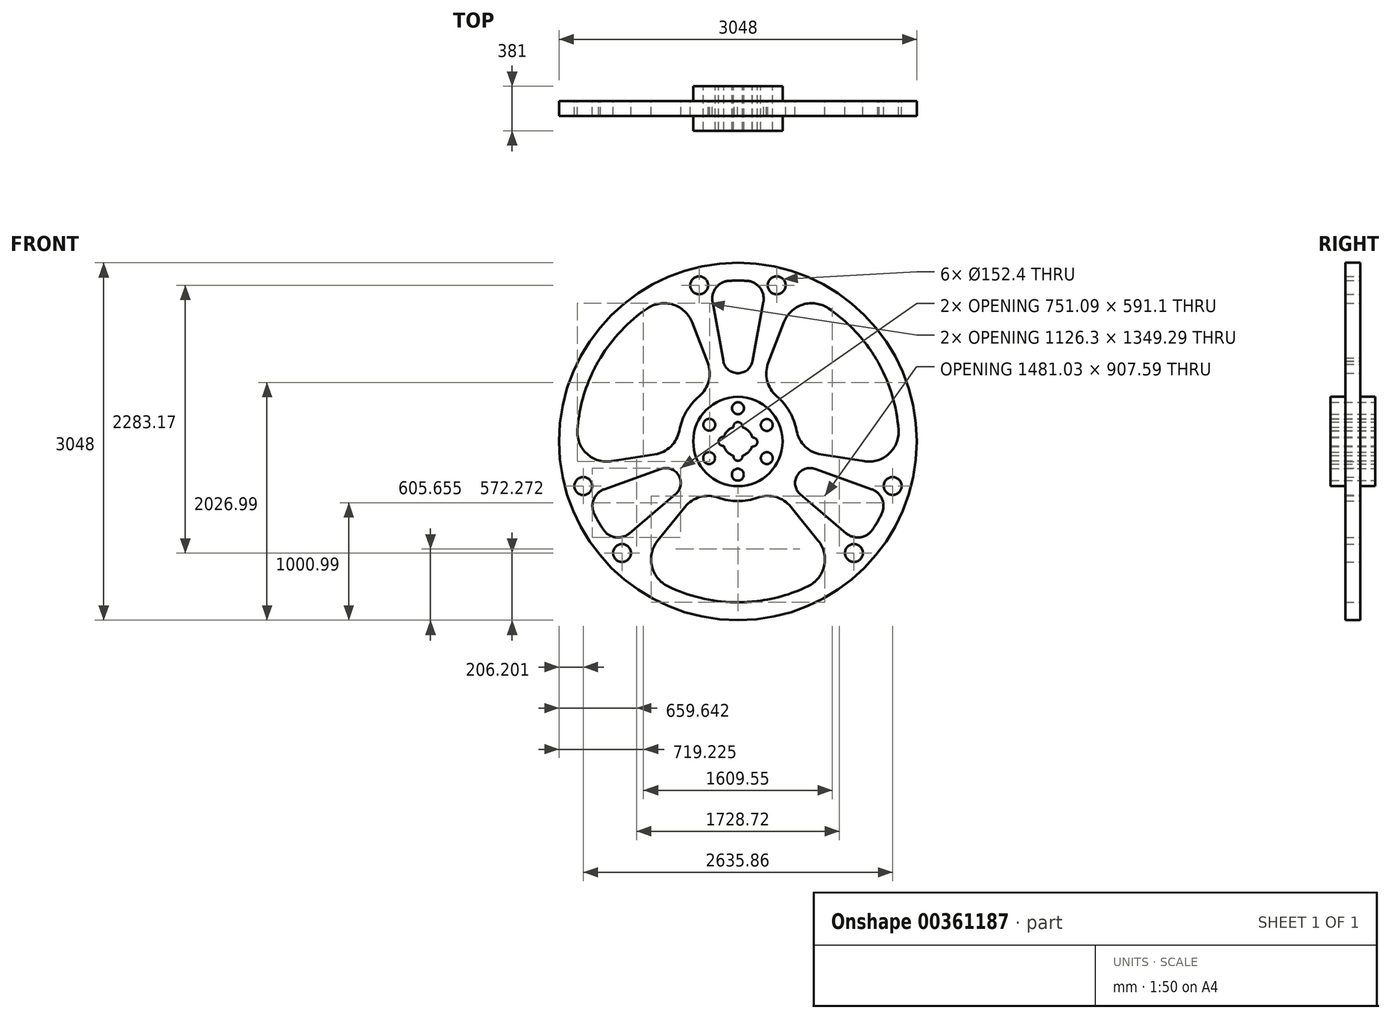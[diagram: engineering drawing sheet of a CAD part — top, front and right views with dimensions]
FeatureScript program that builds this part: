
annotation { "Feature Type Name" : "Feature", "Feature Type Description" : "" }
export const myFeature = defineFeature(function(context is Context, id is Id, definition is map)
    precondition{}
    {
        {
            var Q0;
            Q0=qCreatedBy(makeId("Front.planeOp"),FACE);
            var sketch = newSketch(context, id + "F0", { "sketchPlane" : qUnion([Q0])});
            skArc(sketch, "E0", {"start": v(75.11, 1369.54) * mm, "mid": v(0, 1371.6) * mm, "end": v(-75.11, 1369.54) * mm});
            skCircle(sketch, "E1", {"center": v(0, 0) * mm, "radius": 1524 * mm});
            skLineSegment(sketch, "E2", {"start": v(124.95, 686.17) * mm, "end": v(216.7, 1190.07) * mm});
            skLineSegment(sketch, "E3", {"start": v(-124.95, 686.17) * mm, "end": v(-216.7, 1190.07) * mm});
            skArc(sketch, "E4", {"start": v(216.7, 1190.07) * mm, "mid": v(186.42, 1311.76) * mm, "end": v(75.11, 1369.54) * mm});
            skArc(sketch, "E5", {"start": v(-75.11, 1369.54) * mm, "mid": v(-186.42, 1311.76) * mm, "end": v(-216.7, 1190.07) * mm});
            skArc(sketch, "E6", {"start": v(-124.95, 686.17) * mm, "mid": v(0, 581.92) * mm, "end": v(124.95, 686.17) * mm});
            skLineSegment(sketch, "E7", {"start": v(-0.65, -508) * mm, "end": v(-2.09, -1524) * mm});
            skPoint(sketch, "E7.endSnap0", {"position": v(-2.18, -1372.14) * mm});
            skLineSegment(sketch, "E8", {"start": v(0, 0) * mm, "end": v(-239.47, -296.33) * mm});
            skLineSegment(sketch, "E9", {"start": v(0, 0) * mm, "end": v(239.47, -296.33) * mm});
            skArc(sketch, "E10", {"start": v(-169.33, -478.95) * mm, "mid": v(0, -508) * mm, "end": v(169.33, -478.95) * mm});
            skArc(sketch, "E11", {"start": v(597.09, -1234.82) * mm, "mid": v(734.38, -1061.67) * mm, "end": v(684.07, -846.5) * mm});
            skArc(sketch, "E12", {"start": v(451.56, -558.77) * mm, "mid": v(323.13, -474) * mm, "end": v(169.33, -478.95) * mm});
            skArc(sketch, "E13", {"start": v(-169.33, -478.95) * mm, "mid": v(-323.13, -474) * mm, "end": v(-451.56, -558.77) * mm});
            skArc(sketch, "E14", {"start": v(-684.07, -846.5) * mm, "mid": v(-734.38, -1061.67) * mm, "end": v(-597.09, -1234.82) * mm});
            skLineSegment(sketch, "E15", {"start": v(-94.07, 1367.3) * mm, "end": v(-75.11, 1369.54) * mm});
            skLineSegment(sketch, "E16", {"start": v(75.11, 1369.54) * mm, "end": v(94.07, 1367.3) * mm});
            skPoint(sketch, "E17.orphan", {"position": v(-698.5, 2222.44) * mm});
            skPoint(sketch, "E18.trimOffspring.end.orphan", {"position": v(-292.1, 1604.1) * mm});
            skPoint(sketch, "E19.orphan", {"position": v(0, 1690.94) * mm});
            skPoint(sketch, "E20.trimOffspring.end.orphan", {"position": v(292.1, 1604.17) * mm});
            skPoint(sketch, "E21.orphan", {"position": v(698.5, 2211.47) * mm});
            skCircle(sketch, "E22", {"center": v(-330.38, 1331.22) * mm, "radius": 76.2 * mm});
            skCircle(sketch, "E23", {"center": v(329.48, 1331.44) * mm, "radius": 76.2 * mm});
            skArc(sketch, "E24.trimOffspring", {"start": v(-770.84, 1134.5) * mm, "mid": v(-1187.84, 685.8) * mm, "end": v(-1367.93, 100.31) * mm});
            skLineSegment(sketch, "E25.trimOffspring", {"start": v(451.56, -558.77) * mm, "end": v(684.07, -846.5) * mm});
            skLineSegment(sketch, "E26.trimOffspring", {"start": v(-451.56, -558.77) * mm, "end": v(-684.07, -846.5) * mm});
            skPoint(sketch, "E27.trimOffspring.end.orphan", {"position": v(-1005.48, -1241.52) * mm});
            skPoint(sketch, "E28.trimOffspring.end.orphan", {"position": v(1001.12, -1241.52) * mm});
            skPoint(sketch, "E29.orphan", {"position": v(-2.18, -1585.86) * mm});
            skPoint(sketch, "E30.orphan", {"position": v(0, -47.86) * mm});
            skLineSegment(sketch, "E31", {"start": v(-0.65, -508) * mm, "end": v(-0.43, -333.85) * mm});
            skArc(sketch, "E32.1.0", {"start": v(-1138.98, -407.37) * mm, "mid": v(-1229.23, -494.44) * mm, "end": v(-1223.61, -619.72) * mm});
            skLineSegment(sketch, "E32.1.1", {"start": v(-656.71, -234.88) * mm, "end": v(-1138.98, -407.37) * mm});
            skArc(sketch, "E32.1.2", {"start": v(-531.77, -451.3) * mm, "mid": v(-503.96, -290.96) * mm, "end": v(-656.71, -234.88) * mm});
            skLineSegment(sketch, "E32.1.3", {"start": v(-531.77, -451.3) * mm, "end": v(-922.28, -782.7) * mm});
            skArc(sketch, "E32.1.4", {"start": v(-1148.5, -749.82) * mm, "mid": v(-1042.81, -817.32) * mm, "end": v(-922.28, -782.7) * mm});
            skArc(sketch, "E32.1.5", {"start": v(-1223.61, -619.72) * mm, "mid": v(-1187.84, -685.8) * mm, "end": v(-1148.5, -749.82) * mm});
            skCircle(sketch, "E32.1.6", {"center": v(-987.67, -951.73) * mm, "radius": 76.2 * mm});
            skCircle(sketch, "E32.1.7", {"center": v(-1317.8, -380.39) * mm, "radius": 76.2 * mm});
            skArc(sketch, "E32.2.0", {"start": v(922.28, -782.7) * mm, "mid": v(1042.81, -817.32) * mm, "end": v(1148.5, -749.82) * mm});
            skLineSegment(sketch, "E32.2.1", {"start": v(531.77, -451.3) * mm, "end": v(922.28, -782.7) * mm});
            skArc(sketch, "E32.2.2", {"start": v(656.71, -234.88) * mm, "mid": v(503.96, -290.96) * mm, "end": v(531.77, -451.3) * mm});
            skLineSegment(sketch, "E32.2.3", {"start": v(656.71, -234.88) * mm, "end": v(1138.98, -407.37) * mm});
            skArc(sketch, "E32.2.4", {"start": v(1223.61, -619.72) * mm, "mid": v(1229.23, -494.44) * mm, "end": v(1138.98, -407.37) * mm});
            skArc(sketch, "E32.2.5", {"start": v(1148.5, -749.82) * mm, "mid": v(1187.84, -685.8) * mm, "end": v(1223.61, -619.72) * mm});
            skCircle(sketch, "E32.2.6", {"center": v(1318.06, -379.49) * mm, "radius": 76.2 * mm});
            skCircle(sketch, "E32.2.7", {"center": v(988.32, -951.05) * mm, "radius": 76.2 * mm});
            skArc(sketch, "E33", {"start": v(-597.09, -1234.82) * mm, "mid": v(-306.72, -1334.18) * mm, "end": v(-2.18, -1372.14) * mm});
            skArc(sketch, "E34", {"start": v(-2.18, -1372.14) * mm, "mid": v(305.1, -1336.87) * mm, "end": v(597.09, -1234.82) * mm});
            skArc(sketch, "E35", {"start": v(-0.65, -508) * mm, "mid": v(85.78, -501.92) * mm, "end": v(169.33, -478.95) * mm});
            skArc(sketch, "E36", {"start": v(-169.33, -478.95) * mm, "mid": v(-86.39, -501.57) * mm, "end": v(-0.65, -508) * mm});
            skArc(sketch, "E37.1.0", {"start": v(258.13, 670.44) * mm, "mid": v(248.94, 516.84) * mm, "end": v(330.11, 386.12) * mm});
            skArc(sketch, "E37.1.1", {"start": v(499.45, 92.83) * mm, "mid": v(477.57, 175.97) * mm, "end": v(440.27, 253.44) * mm});
            skArc(sketch, "E37.1.2", {"start": v(440.27, 253.44) * mm, "mid": v(391.78, 325.25) * mm, "end": v(330.11, 386.12) * mm});
            skArc(sketch, "E37.1.3", {"start": v(499.45, 92.83) * mm, "mid": v(572.07, -42.83) * mm, "end": v(709.69, -111.67) * mm});
            skLineSegment(sketch, "E37.1.4", {"start": v(709.69, -111.67) * mm, "end": v(1075.12, -169.18) * mm});
            skArc(sketch, "E37.1.5", {"start": v(1075.12, -169.18) * mm, "mid": v(1286.62, -105.15) * mm, "end": v(1367.93, 100.31) * mm});
            skArc(sketch, "E37.1.6", {"start": v(1367.93, 100.31) * mm, "mid": v(1308.8, 401.46) * mm, "end": v(1189.4, 684.19) * mm});
            skArc(sketch, "E37.1.7", {"start": v(1189.4, 684.19) * mm, "mid": v(1005.2, 932.67) * mm, "end": v(770.84, 1134.5) * mm});
            skArc(sketch, "E37.1.8", {"start": v(770.84, 1134.5) * mm, "mid": v(552.24, 1166.82) * mm, "end": v(391.05, 1015.67) * mm});
            skLineSegment(sketch, "E37.1.9", {"start": v(258.13, 670.44) * mm, "end": v(391.05, 1015.67) * mm});
            skArc(sketch, "E37.2.0", {"start": v(-709.69, -111.67) * mm, "mid": v(-572.07, -42.83) * mm, "end": v(-499.45, 92.83) * mm});
            skArc(sketch, "E37.2.1", {"start": v(-330.11, 386.12) * mm, "mid": v(-391.18, 325.6) * mm, "end": v(-439.62, 254.56) * mm});
            skArc(sketch, "E37.2.2", {"start": v(-439.62, 254.56) * mm, "mid": v(-477.56, 176.67) * mm, "end": v(-499.45, 92.83) * mm});
            skArc(sketch, "E37.2.3", {"start": v(-330.11, 386.12) * mm, "mid": v(-248.94, 516.84) * mm, "end": v(-258.13, 670.44) * mm});
            skLineSegment(sketch, "E37.2.4", {"start": v(-258.13, 670.44) * mm, "end": v(-391.05, 1015.67) * mm});
            skArc(sketch, "E37.2.5", {"start": v(-391.05, 1015.67) * mm, "mid": v(-552.24, 1166.82) * mm, "end": v(-770.84, 1134.5) * mm});
            skArc(sketch, "E37.2.6", {"start": v(-770.84, 1134.5) * mm, "mid": v(-1002.07, 932.72) * mm, "end": v(-1187.22, 687.95) * mm});
            skArc(sketch, "E37.2.7", {"start": v(-1187.22, 687.95) * mm, "mid": v(-1310.32, 404.2) * mm, "end": v(-1367.93, 100.31) * mm});
            skArc(sketch, "E37.2.8", {"start": v(-1367.93, 100.31) * mm, "mid": v(-1286.62, -105.15) * mm, "end": v(-1075.12, -169.18) * mm});
            skLineSegment(sketch, "E37.2.9", {"start": v(-709.69, -111.67) * mm, "end": v(-1075.12, -169.18) * mm});
            skArc(sketch, "E38.trimOffspring", {"start": v(1367.93, 100.31) * mm, "mid": v(1187.84, 685.8) * mm, "end": v(770.84, 1134.5) * mm});
            skArc(sketch, "E39.trimOffspring", {"start": v(-597.09, -1234.82) * mm, "mid": v(0, -1371.6) * mm, "end": v(597.09, -1234.82) * mm});
            skCircle(sketch, "E40", {"center": v(0, 0) * mm, "radius": 381 * mm});
            skArc(sketch, "E41.trimOffspring", {"start": v(-330.11, 386.12) * mm, "mid": v(-439.94, 254) * mm, "end": v(-499.45, 92.83) * mm});
            skArc(sketch, "E42.trimOffspring", {"start": v(499.45, 92.83) * mm, "mid": v(439.94, 254) * mm, "end": v(330.11, 386.12) * mm});
            skArc(sketch, "E43", {"start": v(-37.67, 121.28) * mm, "mid": v(-89.8, 89.8) * mm, "end": v(-121.29, 37.67) * mm});
            skCircle(sketch, "E44", {"center": v(0, 283.57) * mm, "radius": 50.8 * mm});
            skCircle(sketch, "E45.1.0", {"center": v(-245.58, -141.78) * mm, "radius": 50.8 * mm});
            skCircle(sketch, "E45.2.0", {"center": v(245.58, -141.78) * mm, "radius": 50.8 * mm});
            skCircle(sketch, "E46", {"center": v(245.7, 140.56) * mm, "radius": 50.8 * mm});
            skCircle(sketch, "E47.1.0", {"center": v(-244.58, 142.5) * mm, "radius": 50.8 * mm});
            skCircle(sketch, "E47.2.0", {"center": v(-1.12, -283.06) * mm, "radius": 50.8 * mm});
            skArc(sketch, "E48", {"start": v(37.67, 121.29) * mm, "mid": v(0, 165.1) * mm, "end": v(-37.67, 121.28) * mm});
            skArc(sketch, "E49", {"start": v(119.78, -42.2) * mm, "mid": v(164.98, -6.22) * mm, "end": v(122.62, 33.07) * mm});
            skPoint(sketch, "E50.orphan", {"position": v(164.98, -6.22) * mm});
            skArc(sketch, "E51", {"start": v(-37.82, -121.24) * mm, "mid": v(-0.21, -165.1) * mm, "end": v(37.51, -121.33) * mm});
            skArc(sketch, "E52", {"start": v(-121.28, 37.67) * mm, "mid": v(-165.1, 0) * mm, "end": v(-121.28, -37.67) * mm});
            skArc(sketch, "E53.trimOffspring", {"start": v(122.62, 33.07) * mm, "mid": v(91.48, 88.1) * mm, "end": v(37.67, 121.29) * mm});
            skArc(sketch, "E54.trimOffspring", {"start": v(37.51, -121.33) * mm, "mid": v(88.04, -91.53) * mm, "end": v(119.78, -42.2) * mm});
            skArc(sketch, "E55.trimOffspring", {"start": v(-121.28, -37.67) * mm, "mid": v(-89.86, -89.75) * mm, "end": v(-37.82, -121.24) * mm});
            skSolve(sketch);
        }
        {
            var Q0;
            Q0 = qSketchRegion(id + "F0", true);
            extrude(context, id + "F1", {"entities" : qUnion([Q0]), "depth" : 127 * mm, "symmetric" : true});
        }
        {
            var Q0;
            Q0=makeQuery(id+"F0.imprint","IMPRINT",FACE,{"disambiguationData":[TD([[makeQuery(id+"F0.imprint","IMPRINT",EDGE,{"derivedFrom":sQuery(id+"F0.wireOp",EDGE,"E43")}),-1.0]])]});
            var Q1;
            Q1=makeQuery(id+"F0.imprint","IMPRINT",FACE,{"disambiguationData":[TD([[makeQuery(id+"F0.imprint","IMPRINT",EDGE,{"derivedFrom":sQuery(id+"F0.wireOp",EDGE,"E47.2.0")}),-1.0]])]});
            extrude(context, id + "F2", {"entities" : qUnion([Q0, Q1]), "operationType" : NewBodyOperationType.ADD, "depth" : 381 * mm, "symmetric" : true});
        }
    });
